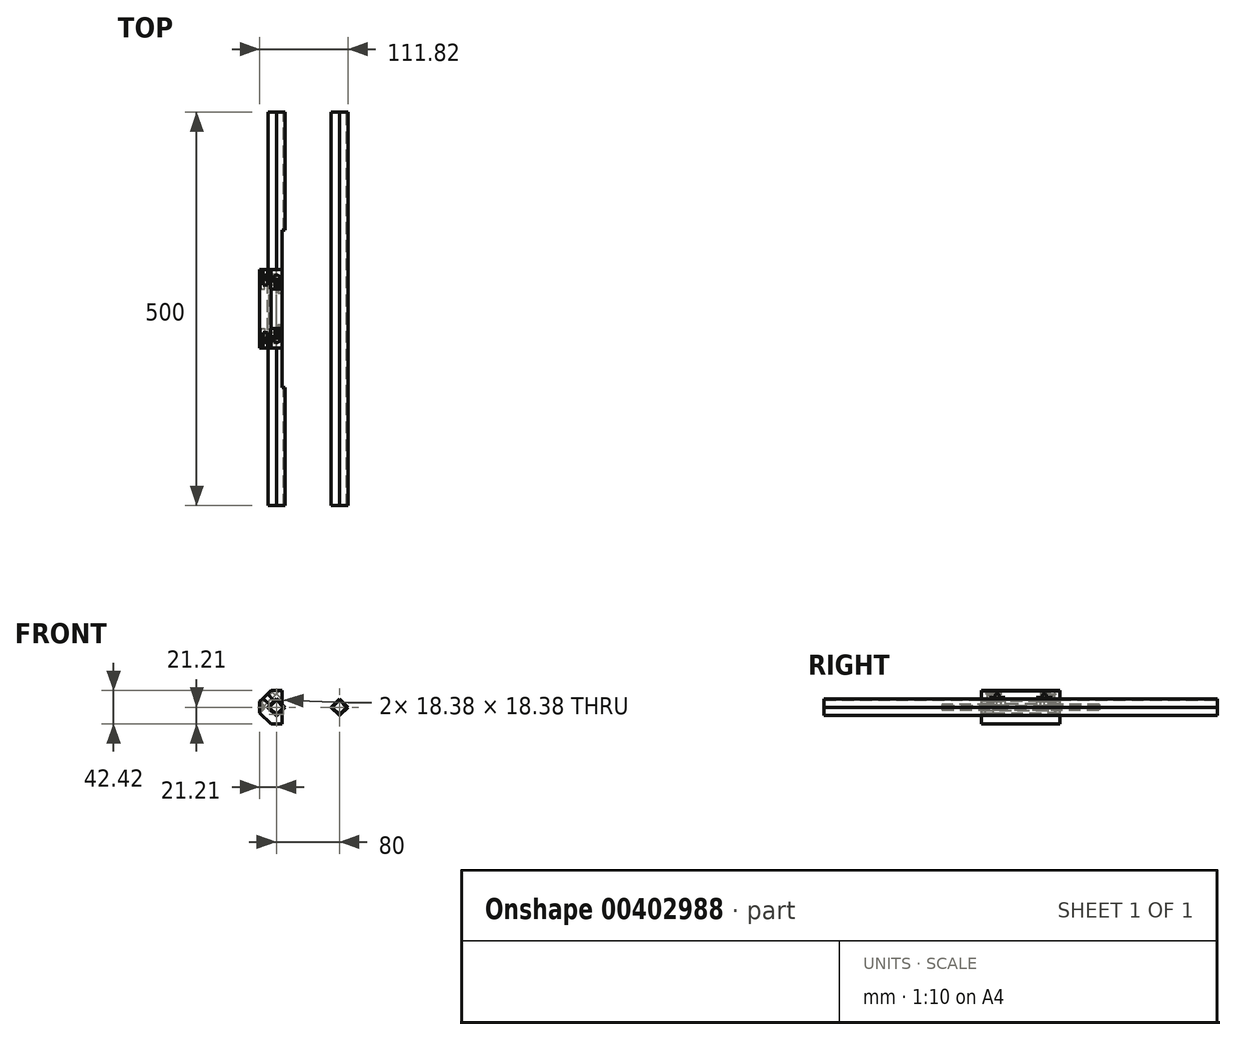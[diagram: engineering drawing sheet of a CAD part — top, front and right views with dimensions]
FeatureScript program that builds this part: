
annotation { "Feature Type Name" : "Feature", "Feature Type Description" : "" }
export const myFeature = defineFeature(function(context is Context, id is Id, definition is map)
    precondition{}
    {
        {
            var Q0;
            Q0=qCreatedBy(makeId("Front.planeOp"),FACE);
            var sketch = newSketch(context, id + "F0", { "sketchPlane" : qUnion([Q0])});
            skCircle(sketch, "E0.cCircle", {"center": v(-40, 0) * mm, "radius": 10.6 * mm, "construction": true});
            skLineSegment(sketch, "E0.0", {"start": v(-40, 10.6) * mm, "end": v(-29.4, 0) * mm});
            skLineSegment(sketch, "E0.1", {"start": v(-29.4, 0) * mm, "end": v(-40, -10.6) * mm});
            skLineSegment(sketch, "E0.2", {"start": v(-40, -10.6) * mm, "end": v(-50.6, 0) * mm});
            skLineSegment(sketch, "E0.3", {"start": v(-50.6, 0) * mm, "end": v(-40, 10.6) * mm});
            skLineSegment(sketch, "E1", {"start": v(-40, 0) * mm, "end": v(-40, 32.5) * mm, "construction": true});
            skLineSegment(sketch, "E2.0", {"start": v(-40, -9.2) * mm, "end": v(-49.2, 0) * mm});
            skLineSegment(sketch, "E2.1", {"start": v(-30.8, 0) * mm, "end": v(-40, -9.2) * mm});
            skLineSegment(sketch, "E2.2", {"start": v(-40, 9.2) * mm, "end": v(-30.8, 0) * mm});
            skLineSegment(sketch, "E2.3", {"start": v(-49.2, 0) * mm, "end": v(-40, 9.2) * mm});
            skLineSegment(sketch, "E3.MirrorCS", {"start": v(40, 10.6) * mm, "end": v(29.4, 0) * mm});
            skLineSegment(sketch, "E4.MirrorCS", {"start": v(40, 9.2) * mm, "end": v(30.8, 0) * mm});
            skLineSegment(sketch, "E5.MirrorCS", {"start": v(50.6, 0) * mm, "end": v(40, 10.6) * mm});
            skLineSegment(sketch, "E6.MirrorCS", {"start": v(49.2, 0) * mm, "end": v(40, 9.2) * mm});
            skLineSegment(sketch, "E7.MirrorCS", {"start": v(40, -9.2) * mm, "end": v(49.2, 0) * mm});
            skLineSegment(sketch, "E8.MirrorCS", {"start": v(40, -10.6) * mm, "end": v(50.6, 0) * mm});
            skLineSegment(sketch, "E9.MirrorCS", {"start": v(30.8, 0) * mm, "end": v(40, -9.2) * mm});
            skLineSegment(sketch, "E10.MirrorCS", {"start": v(29.4, 0) * mm, "end": v(40, -10.6) * mm});
            skSolve(sketch);
        }
        {
            var Q0;
            Q0 = qSketchRegion(id + "F0", true);
            extrude(context, id + "F1", {"entities" : qUnion([Q0]), "endBound" : BoundingType.SYMMETRIC, "depth" : 500 * mm});
        }
        {
            var Q0;
            Q0=qCreatedBy(makeId("Front.planeOp"),FACE);
            var sketch = newSketch(context, id + "F2", { "sketchPlane" : qUnion([Q0])});
            skLineSegment(sketch, "E11", {"start": v(-40, 16.2) * mm, "end": v(-40, -28.91) * mm, "construction": true});
            skLineSegment(sketch, "E12", {"start": v(-40, 0) * mm, "end": v(-64.43, 24.43) * mm, "construction": true});
            skLineSegment(sketch, "E13.0", {"start": v(-51.31, 0) * mm, "end": v(-40, 11.31) * mm});
            skLineSegment(sketch, "E13.1", {"start": v(-40, -11.31) * mm, "end": v(-51.31, 0) * mm});
            skLineSegment(sketch, "E13.2", {"start": v(-28.69, 0) * mm, "end": v(-40, -11.31) * mm});
            skLineSegment(sketch, "E13.3", {"start": v(-40, 11.31) * mm, "end": v(-28.69, 0) * mm});
            skLineSegment(sketch, "E14.0", {"start": v(-40, 28.28) * mm, "end": v(-11.72, 0) * mm});
            skLineSegment(sketch, "E14.1", {"start": v(-68.28, 0) * mm, "end": v(-40, 28.28) * mm});
            skLineSegment(sketch, "E14.2", {"start": v(-40, -28.28) * mm, "end": v(-68.28, 0) * mm});
            skLineSegment(sketch, "E14.3", {"start": v(-11.72, 0) * mm, "end": v(-40, -28.28) * mm});
            skSolve(sketch);
        }
        {
            var Q0;
            Q0 = qSketchRegion(id + "F2", true);
            extrude(context, id + "F3", {"entities" : qUnion([Q0]), "endBound" : BoundingType.SYMMETRIC, "depth" : 100 * mm});
        }
        {
            var Q0;
            Q0=makeQuery(id+"F3.opExtrude","SWEPT_FACE",FACE,{"disambiguationData":[OSD([sQuery(id+"F2.wireOp",EDGE,"E14.2")])]});
            var sketch = newSketch(context, id + "F4", { "sketchPlane" : qUnion([Q0])});
            skLineSegment(sketch, "E15", {"start": v(-50, 42.98) * mm, "end": v(50, 42.98) * mm, "construction": true});
            skLineSegment(sketch, "E16", {"start": v(-50, 28.28) * mm, "end": v(50, 28.28) * mm, "construction": true});
            skCircle(sketch, "E17", {"center": v(-40, 42.98) * mm, "radius": 2.7 * mm});
            skCircle(sketch, "E18.MirrorC", {"center": v(40, 42.98) * mm, "radius": 2.7 * mm});
            skSolve(sketch);
        }
        {
            var Q0;
            Q0 = qSketchRegion(id + "F4", true);
            extrude(context, id + "F5", {"entities" : qUnion([Q0]), "operationType" : NewBodyOperationType.REMOVE, "oppositeDirection" : true, "depth" : 70 * mm});
        }
        {
            var Q0;
            Q0=makeQuery(id+"F3.opExtrude","SWEPT_FACE",FACE,{"disambiguationData":[OSD([sQuery(id+"F2.wireOp",EDGE,"E14.1")])]});
            var sketch = newSketch(context, id + "F6", { "sketchPlane" : qUnion([Q0])});
            skLineSegment(sketch, "E19", {"start": v(-50, -28.28) * mm, "end": v(50, -28.28) * mm, "construction": true});
            skLineSegment(sketch, "E20", {"start": v(-50, -13.58) * mm, "end": v(50, -13.58) * mm, "construction": true});
            skCircle(sketch, "E21", {"center": v(-30, -13.58) * mm, "radius": 2.7 * mm});
            skCircle(sketch, "E22.MirrorC", {"center": v(30, -13.58) * mm, "radius": 2.7 * mm});
            skSolve(sketch);
        }
        {
            var Q0;
            Q0 = qSketchRegion(id + "F6", true);
            extrude(context, id + "F7", {"entities" : qUnion([Q0]), "operationType" : NewBodyOperationType.REMOVE, "oppositeDirection" : true, "depth" : 60 * mm});
        }
        {
            var Q0;
            Q0=makeQuery(id+"F3.opExtrude","SWEPT_FACE",FACE,{"disambiguationData":[OSD([sQuery(id+"F2.wireOp",EDGE,"E14.1")])]});
            var sketch = newSketch(context, id + "F8", { "sketchPlane" : qUnion([Q0])});
            skLineSegment(sketch, "E23", {"start": v(-50, -28.28) * mm, "end": v(50, -28.28) * mm, "construction": true});
            skLineSegment(sketch, "E24.bottom", {"start": v(-30, -32.03) * mm, "end": v(-50, -32.03) * mm});
            skLineSegment(sketch, "E24.top", {"start": v(-30, -24.53) * mm, "end": v(-50, -24.53) * mm});
            skLineSegment(sketch, "E24.left", {"start": v(-30, -32.03) * mm, "end": v(-30, -24.53) * mm});
            skLineSegment(sketch, "E24.right", {"start": v(-50, -32.03) * mm, "end": v(-50, -24.53) * mm});
            skPoint(sketch, "E24.middle", {"position": v(-40, -28.28) * mm});
            skLineSegment(sketch, "E25.MirrorCS", {"start": v(30, -32.03) * mm, "end": v(30, -24.53) * mm});
            skLineSegment(sketch, "E26.MirrorCS", {"start": v(30, -24.53) * mm, "end": v(50, -24.53) * mm});
            skLineSegment(sketch, "E27.MirrorCS", {"start": v(50, -32.03) * mm, "end": v(50, -24.53) * mm});
            skLineSegment(sketch, "E28.MirrorCS", {"start": v(30, -32.03) * mm, "end": v(50, -32.03) * mm});
            skSolve(sketch);
        }
        {
            var Q0;
            Q0 = qSketchRegion(id + "F8", true);
            extrude(context, id + "F9", {"entities" : qUnion([Q0]), "operationType" : NewBodyOperationType.REMOVE, "oppositeDirection" : true, "depth" : 20 * mm});
        }
        {
            var Q0;
            Q0=makeQuery(id+"F3.opExtrude","SWEPT_FACE",FACE,{"disambiguationData":[OSD([sQuery(id+"F2.wireOp",EDGE,"E14.0")])]});
            var sketch = newSketch(context, id + "F10", { "sketchPlane" : qUnion([Q0])});
            skLineSegment(sketch, "E29", {"start": v(50, 28.28) * mm, "end": v(-50, 28.28) * mm, "construction": true});
            skLineSegment(sketch, "E30.bottom", {"start": v(20, 32.03) * mm, "end": v(40, 32.03) * mm});
            skLineSegment(sketch, "E30.top", {"start": v(20, 24.53) * mm, "end": v(40, 24.53) * mm});
            skLineSegment(sketch, "E30.left", {"start": v(20, 32.03) * mm, "end": v(20, 24.53) * mm});
            skLineSegment(sketch, "E30.right", {"start": v(40, 32.03) * mm, "end": v(40, 24.53) * mm});
            skPoint(sketch, "E30.middle", {"position": v(30, 28.28) * mm});
            skLineSegment(sketch, "E31.MirrorCS", {"start": v(-20, 32.03) * mm, "end": v(-20, 24.53) * mm});
            skLineSegment(sketch, "E32.MirrorCS", {"start": v(-20, 24.53) * mm, "end": v(-40, 24.53) * mm});
            skLineSegment(sketch, "E33.MirrorCS", {"start": v(-40, 32.03) * mm, "end": v(-40, 24.53) * mm});
            skLineSegment(sketch, "E34.MirrorCS", {"start": v(-20, 32.03) * mm, "end": v(-40, 32.03) * mm});
            skSolve(sketch);
        }
        {
            var Q0;
            Q0 = qSketchRegion(id + "F10", true);
            extrude(context, id + "F11", {"entities" : qUnion([Q0]), "operationType" : NewBodyOperationType.REMOVE, "oppositeDirection" : true, "depth" : 20 * mm});
        }
        {
            var Q0;
            Q0=makeQuery(id+"F3.opExtrude","SWEPT_FACE",FACE,{"disambiguationData":[OSD([sQuery(id+"F2.wireOp",EDGE,"E14.2")])]});
            cPlane(context, id + "F12", {"entities" : qUnion([Q0]), "cplaneType" : CPlaneType.OFFSET, "offset" : 20 * mm, "oppositeDirection" : true, "width" : 150 * mm, "height" : 150 * mm});
        }
        {
            var Q0;
            Q0=makeQuery(id+"F3.opExtrude","SWEPT_EDGE",EDGE,{"disambiguationData":[OSD([sQuery(id+"F2.wireOp",EDGE,"E14.2"),sQuery(id+"F2.wireOp",EDGE,"E14.3")])]});
            var Q1;
            Q1=makeQuery(id+"F3.opExtrude","SWEPT_EDGE",EDGE,{"disambiguationData":[OSD([sQuery(id+"F2.wireOp",EDGE,"E14.0"),sQuery(id+"F2.wireOp",EDGE,"E14.3")])]});
            chamfer(context, id + "F13", {"entities" : qUnion([Q0, Q1]), "width" : 10 * mm, "tangentPropagation" : true});
        }
        {
            var Q0;
            Q0=makeQuery(id+"F3.opExtrude","SWEPT_EDGE",EDGE,{"disambiguationData":[OSD([sQuery(id+"F2.wireOp",EDGE,"E14.0"),sQuery(id+"F2.wireOp",EDGE,"E14.1")])]});
            var Q1;
            Q1=makeQuery(id+"F3.opExtrude","SWEPT_EDGE",EDGE,{"disambiguationData":[OSD([sQuery(id+"F2.wireOp",EDGE,"E14.1"),sQuery(id+"F2.wireOp",EDGE,"E14.2")])]});
            chamfer(context, id + "F14", {"entities" : qUnion([Q0, Q1]), "width" : 10 * mm, "tangentPropagation" : true});
        }
        {
            var Q0;
            Q0=qCreatedBy(id+"F12.planeOp",FACE);
            cPlane(context, id + "F15", {"entities" : qUnion([Q0]), "cplaneType" : CPlaneType.OFFSET, "offset" : 12 * mm, "width" : 150 * mm, "height" : 150 * mm});
        }
        {
            var Q0;
            Q0=qCreatedBy(id+"F15.planeOp",FACE);
            var sketch = newSketch(context, id + "F16", { "sketchPlane" : qUnion([Q0])});
            skCircle(sketch, "E35", {"center": v(-40, 42.98) * mm, "radius": 5 * mm, "construction": true});
            skCircle(sketch, "E36", {"center": v(40, 42.98) * mm, "radius": 5 * mm, "construction": true});
            skLineSegment(sketch, "E37.bottom", {"start": v(-35, 37.98) * mm, "end": v(-45, 37.98) * mm});
            skLineSegment(sketch, "E37.top", {"start": v(-35, 47.98) * mm, "end": v(-45, 47.98) * mm});
            skLineSegment(sketch, "E37.left", {"start": v(-35, 37.98) * mm, "end": v(-35, 47.98) * mm});
            skLineSegment(sketch, "E37.right", {"start": v(-45, 37.98) * mm, "end": v(-45, 47.98) * mm});
            skLineSegment(sketch, "E38.MirrorCS", {"start": v(35, 37.98) * mm, "end": v(35, 47.98) * mm});
            skLineSegment(sketch, "E39.MirrorCS", {"start": v(35, 37.98) * mm, "end": v(45, 37.98) * mm});
            skLineSegment(sketch, "E40.MirrorCS", {"start": v(45, 37.98) * mm, "end": v(45, 47.98) * mm});
            skLineSegment(sketch, "E41.MirrorCS", {"start": v(35, 47.98) * mm, "end": v(45, 47.98) * mm});
            skSolve(sketch);
        }
        {
            var Q0;
            Q0 = qSketchRegion(id + "F16", true);
            extrude(context, id + "F17", {"entities" : qUnion([Q0]), "operationType" : NewBodyOperationType.REMOVE, "depth" : 25 * mm});
        }
        {
            var Q0;
            Q0=makeQuery(id+"F3.opExtrude","SWEPT_FACE",FACE,{"disambiguationData":[OSD([sQuery(id+"F2.wireOp",EDGE,"E14.1")])]});
            cPlane(context, id + "F18", {"entities" : qUnion([Q0]), "cplaneType" : CPlaneType.OFFSET, "offset" : 20 * mm, "oppositeDirection" : true, "width" : 150 * mm, "height" : 150 * mm});
        }
        {
            var Q0;
            Q0=qCreatedBy(id+"F18.planeOp",FACE);
            cPlane(context, id + "F19", {"entities" : qUnion([Q0]), "cplaneType" : CPlaneType.OFFSET, "offset" : 12 * mm, "width" : 150 * mm, "height" : 150 * mm});
        }
        {
            var Q0;
            Q0=qCreatedBy(id+"F19.planeOp",FACE);
            var sketch = newSketch(context, id + "F20", { "sketchPlane" : qUnion([Q0])});
            skCircle(sketch, "E42", {"center": v(-30, -13.58) * mm, "radius": 5 * mm, "construction": true});
            skCircle(sketch, "E43", {"center": v(30, -13.58) * mm, "radius": 5 * mm, "construction": true});
            skCircle(sketch, "E44", {"center": v(-30, -42.98) * mm, "radius": 5 * mm, "construction": true});
            skCircle(sketch, "E45", {"center": v(30, -42.98) * mm, "radius": 5 * mm, "construction": true});
            skLineSegment(sketch, "E46.bottom", {"start": v(-25, -8.58) * mm, "end": v(-35, -8.58) * mm});
            skLineSegment(sketch, "E46.top", {"start": v(-25, -18.58) * mm, "end": v(-35, -18.58) * mm});
            skLineSegment(sketch, "E46.left", {"start": v(-25, -8.58) * mm, "end": v(-25, -18.58) * mm});
            skLineSegment(sketch, "E46.right", {"start": v(-35, -8.58) * mm, "end": v(-35, -18.58) * mm});
            skLineSegment(sketch, "E47.MirrorCS", {"start": v(25, -8.58) * mm, "end": v(25, -18.58) * mm});
            skLineSegment(sketch, "E48.MirrorCS", {"start": v(25, -8.58) * mm, "end": v(35, -8.58) * mm});
            skLineSegment(sketch, "E49.MirrorCS", {"start": v(35, -8.58) * mm, "end": v(35, -18.58) * mm});
            skLineSegment(sketch, "E50.MirrorCS", {"start": v(25, -18.58) * mm, "end": v(35, -18.58) * mm});
            skLineSegment(sketch, "E51.MirrorCS", {"start": v(-35, -47.98) * mm, "end": v(-35, -37.98) * mm});
            skLineSegment(sketch, "E52.MirrorCS", {"start": v(-25, -37.98) * mm, "end": v(-35, -37.98) * mm});
            skLineSegment(sketch, "E53.MirrorCS", {"start": v(-25, -47.98) * mm, "end": v(-25, -37.98) * mm});
            skLineSegment(sketch, "E54.MirrorCS", {"start": v(-25, -47.98) * mm, "end": v(-35, -47.98) * mm});
            skLineSegment(sketch, "E55.MirrorCS", {"start": v(25, -47.98) * mm, "end": v(25, -37.98) * mm});
            skLineSegment(sketch, "E56.MirrorCS", {"start": v(25, -47.98) * mm, "end": v(35, -47.98) * mm});
            skLineSegment(sketch, "E57.MirrorCS", {"start": v(35, -47.98) * mm, "end": v(35, -37.98) * mm});
            skLineSegment(sketch, "E58.MirrorCS", {"start": v(25, -37.98) * mm, "end": v(35, -37.98) * mm});
            skSolve(sketch);
        }
        {
            var Q0;
            Q0 = qSketchRegion(id + "F20", true);
            extrude(context, id + "F21", {"entities" : qUnion([Q0]), "operationType" : NewBodyOperationType.REMOVE, "depth" : 25 * mm});
        }
        {
            var Q0;
            Q0=qCreatedBy(makeId("Front.planeOp"),FACE);
            var sketch = newSketch(context, id + "F22", { "sketchPlane" : qUnion([Q0])});
            skLineSegment(sketch, "E59.bottom", {"start": v(-32.72, 41.9) * mm, "end": v(0, 41.9) * mm});
            skLineSegment(sketch, "E59.top", {"start": v(-32.72, -45.93) * mm, "end": v(0, -45.93) * mm});
            skLineSegment(sketch, "E59.left", {"start": v(-32.72, 41.9) * mm, "end": v(-32.72, -45.93) * mm});
            skLineSegment(sketch, "E59.right", {"start": v(0, 41.9) * mm, "end": v(0, -45.93) * mm});
            skSolve(sketch);
        }
        {
            var Q0;
            Q0 = qSketchRegion(id + "F22", true);
            extrude(context, id + "F23", {"entities" : qUnion([Q0]), "operationType" : NewBodyOperationType.REMOVE, "endBound" : BoundingType.SYMMETRIC, "oppositeDirection" : true, "depth" : 200 * mm});
        }
    });
